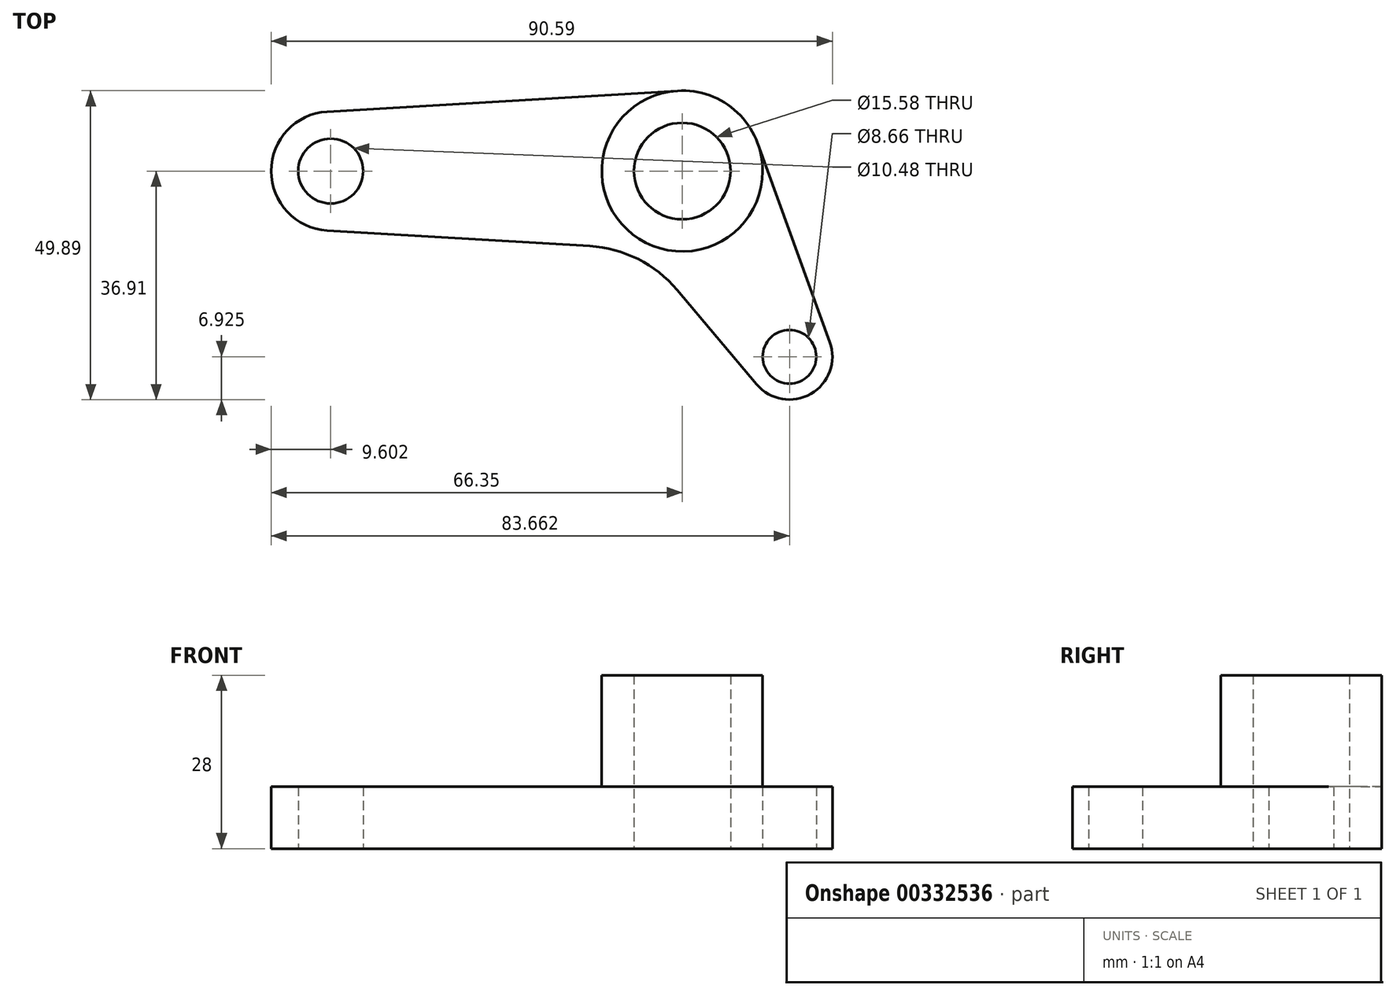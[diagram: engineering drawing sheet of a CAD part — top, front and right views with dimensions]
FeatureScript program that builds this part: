
annotation { "Feature Type Name" : "Feature", "Feature Type Description" : "" }
export const myFeature = defineFeature(function(context is Context, id is Id, definition is map)
    precondition{}
    {
        {
            var Q0;
            Q0=qCreatedBy(makeId("Top.planeOp"),FACE);
            var sketch = newSketch(context, id + "F0", { "sketchPlane" : qUnion([Q0])});
            skCircle(sketch, "E0", {"center": v(0, 0) * mm, "radius": 7.8 * mm});
            skCircle(sketch, "E1", {"center": v(0, 0) * mm, "radius": 12.98 * mm});
            skArc(sketch, "E2", {"start": v(12.01, -34.44) * mm, "mid": v(20.77, -35.98) * mm, "end": v(23.82, -27.63) * mm});
            skCircle(sketch, "E3", {"center": v(17.31, -29.98) * mm, "radius": 4.33 * mm});
            skCircle(sketch, "E4", {"center": v(-56.75, 0) * mm, "radius": 5.24 * mm});
            skArc(sketch, "E5", {"start": v(-57.32, 9.59) * mm, "mid": v(-66.35, 0) * mm, "end": v(-57.32, -9.59) * mm});
            skLineSegment(sketch, "E6", {"start": v(-57.32, -9.59) * mm, "end": v(-14.92, -12.12) * mm});
            skLineSegment(sketch, "E7", {"start": v(-57.32, 9.59) * mm, "end": v(-0.37, 12.98) * mm});
            skLineSegment(sketch, "E8", {"start": v(12.2, 4.42) * mm, "end": v(23.82, -27.63) * mm});
            skArc(sketch, "E9", {"start": v(-0.8, -19.2) * mm, "mid": v(-7.14, -14.2) * mm, "end": v(-14.92, -12.12) * mm});
            skLineSegment(sketch, "E10.trimOffspring", {"start": v(-0.8, -19.2) * mm, "end": v(12.01, -34.44) * mm});
            skSolve(sketch);
        }
        {
            var Q0;
            Q0=makeQuery(id+"F0.imprint","IMPRINT",FACE,{"disambiguationData":[TD([[makeQuery(id+"F0.imprint","IMPRINT",EDGE,{"derivedFrom":sQuery(id+"F0.wireOp",EDGE,"E0")}),-1.0]])]});
            extrude(context, id + "F1", {"entities" : qUnion([Q0]), "depth" : 28 * mm});
        }
        {
            var Q0;
            Q0=makeQuery(id+"F0.imprint","IMPRINT",FACE,{"disambiguationData":[TD([[makeQuery(id+"F0.imprint","IMPRINT",EDGE,{"derivedFrom":sQuery(id+"F0.wireOp",EDGE,"E2")}),1.0]])]});
            extrude(context, id + "F2", {"entities" : qUnion([Q0]), "operationType" : NewBodyOperationType.ADD, "depth" : 10 * mm});
        }
    });
